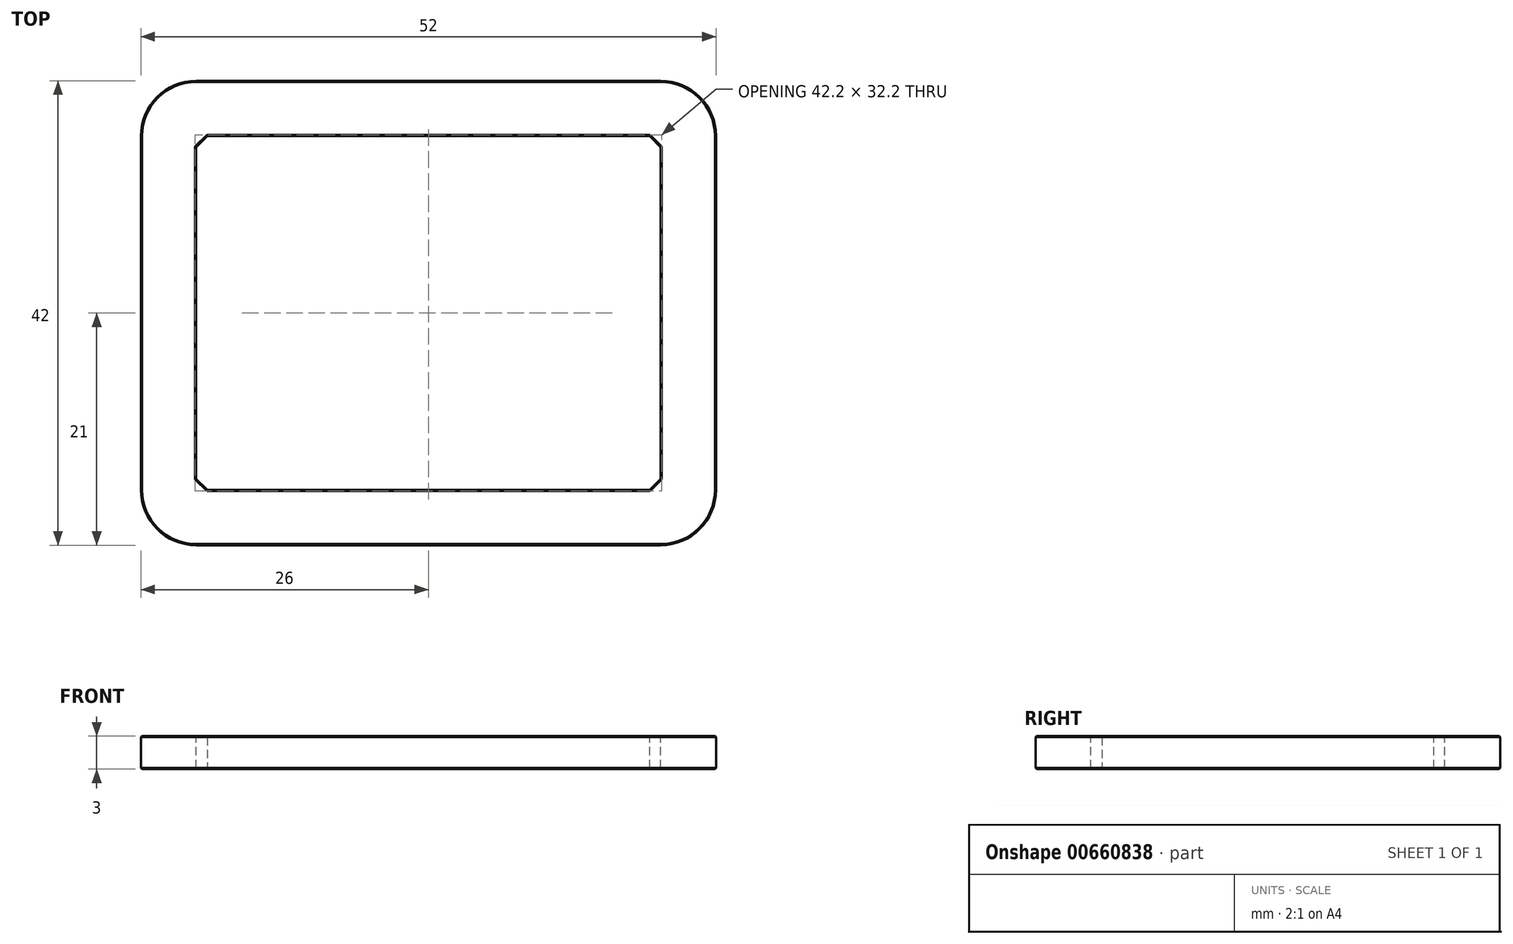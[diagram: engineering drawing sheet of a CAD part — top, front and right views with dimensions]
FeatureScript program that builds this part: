
annotation { "Feature Type Name" : "Feature", "Feature Type Description" : "" }
export const myFeature = defineFeature(function(context is Context, id is Id, definition is map)
    precondition{}
    {
        {
            var Q0;
            Q0=qCreatedBy(makeId("Top.planeOp"),FACE);
            var sketch = newSketch(context, id + "F0", { "sketchPlane" : qUnion([Q0])});
            skLineSegment(sketch, "E0.bottom", {"start": v(-26, 21) * mm, "end": v(26, 21) * mm});
            skLineSegment(sketch, "E0.top", {"start": v(-26, -21) * mm, "end": v(26, -21) * mm});
            skLineSegment(sketch, "E0.left", {"start": v(-26, 21) * mm, "end": v(-26, -21) * mm});
            skLineSegment(sketch, "E0.right", {"start": v(26, 21) * mm, "end": v(26, -21) * mm});
            skPoint(sketch, "E0.middle", {"position": v(0, 0) * mm});
            skLineSegment(sketch, "E1.bottom", {"start": v(-21, 16) * mm, "end": v(21, 16) * mm});
            skLineSegment(sketch, "E1.top", {"start": v(-21, -16) * mm, "end": v(21, -16) * mm});
            skLineSegment(sketch, "E1.left", {"start": v(-21, 16) * mm, "end": v(-21, -16) * mm});
            skLineSegment(sketch, "E1.right", {"start": v(21, 16) * mm, "end": v(21, -16) * mm});
            skSolve(sketch);
        }
        {
            var Q0;
            Q0=makeQuery(id+"F0.imprint","IMPRINT",FACE,{"disambiguationData":[TD([[makeQuery(id+"F0.imprint","IMPRINT",EDGE,{"derivedFrom":sQuery(id+"F0.wireOp",EDGE,"E0.bottom")}),-1.0]])]});
            extrude(context, id + "F1", {"entities" : qUnion([Q0]), "depth" : 3 * mm, "offsetDistance" : 25 * mm});
        }
        {
            var Q0;
            Q0=makeQuery(id+"F1.opExtrude","SWEPT_EDGE",EDGE,{"disambiguationData":[OSD([sQuery(id+"F0.wireOp",EDGE,"E0.bottom"),sQuery(id+"F0.wireOp",EDGE,"E0.left")])]});
            var Q1;
            Q1=makeQuery(id+"F1.opExtrude","SWEPT_EDGE",EDGE,{"disambiguationData":[OSD([sQuery(id+"F0.wireOp",EDGE,"E0.top"),sQuery(id+"F0.wireOp",EDGE,"E0.left")])]});
            var Q2;
            Q2=makeQuery(id+"F1.opExtrude","SWEPT_EDGE",EDGE,{"disambiguationData":[OSD([sQuery(id+"F0.wireOp",EDGE,"E0.top"),sQuery(id+"F0.wireOp",EDGE,"E0.right")])]});
            var Q3;
            Q3=makeQuery(id+"F1.opExtrude","SWEPT_EDGE",EDGE,{"disambiguationData":[OSD([sQuery(id+"F0.wireOp",EDGE,"E0.bottom"),sQuery(id+"F0.wireOp",EDGE,"E0.right")])]});
            fillet(context, id + "F2", {"entities" : qUnion([Q0, Q1, Q2, Q3]), "radius" : 5 * mm, "tangentPropagation" : true, "allowEdgeOverflow" : false});
        }
        {
            var Q0;
            Q0=makeQuery(id+"F1.opExtrude","SWEPT_EDGE",EDGE,{"disambiguationData":[OSD([sQuery(id+"F0.wireOp",EDGE,"E1.bottom"),sQuery(id+"F0.wireOp",EDGE,"E1.left")])]});
            chamfer(context, id + "F3", {"entities" : qUnion([Q0]), "chamferType" : ChamferType.TWO_OFFSETS, "width1" : 1 * mm, "oppositeDirection" : true, "width2" : 1 * mm, "tangentPropagation" : true});
        }
        {
            var Q0;
            Q0=makeQuery(id+"F1.opExtrude","SWEPT_EDGE",EDGE,{"disambiguationData":[OSD([sQuery(id+"F0.wireOp",EDGE,"E1.bottom"),sQuery(id+"F0.wireOp",EDGE,"E1.right")])]});
            var Q1;
            Q1=makeQuery(id+"F1.opExtrude","SWEPT_EDGE",EDGE,{"disambiguationData":[OSD([sQuery(id+"F0.wireOp",EDGE,"E1.top"),sQuery(id+"F0.wireOp",EDGE,"E1.right")])]});
            var Q2;
            Q2=makeQuery(id+"F1.opExtrude","SWEPT_EDGE",EDGE,{"disambiguationData":[OSD([sQuery(id+"F0.wireOp",EDGE,"E1.top"),sQuery(id+"F0.wireOp",EDGE,"E1.left")])]});
            chamfer(context, id + "F4", {"entities" : qUnion([Q0, Q1, Q2]), "width" : 1 * mm, "tangentPropagation" : true});
        }
        {
            var Q0;
            Q0=makeQuery(id+"F1.opExtrude","CAP_FACE",FACE,{"disambiguationData":[OSD([sQuery(id+"F0.wireOp",EDGE,"E0.bottom"),sQuery(id+"F0.wireOp",EDGE,"E0.top"),sQuery(id+"F0.wireOp",EDGE,"E0.left"),sQuery(id+"F0.wireOp",EDGE,"E0.right"),sQuery(id+"F0.wireOp",EDGE,"E1.bottom"),sQuery(id+"F0.wireOp",EDGE,"E1.top"),sQuery(id+"F0.wireOp",EDGE,"E1.left"),sQuery(id+"F0.wireOp",EDGE,"E1.right")])],"isStart":false});
            var Q1;
            Q1=makeQuery(id+"F1.opExtrude","CAP_FACE",FACE,{"disambiguationData":[OSD([sQuery(id+"F0.wireOp",EDGE,"E0.bottom"),sQuery(id+"F0.wireOp",EDGE,"E0.top"),sQuery(id+"F0.wireOp",EDGE,"E0.left"),sQuery(id+"F0.wireOp",EDGE,"E0.right"),sQuery(id+"F0.wireOp",EDGE,"E1.bottom"),sQuery(id+"F0.wireOp",EDGE,"E1.top"),sQuery(id+"F0.wireOp",EDGE,"E1.left"),sQuery(id+"F0.wireOp",EDGE,"E1.right")])],"isStart":true});
            chamfer(context, id + "F5", {"entities" : qUnion([Q0, Q1]), "width" : 0.1 * mm, "tangentPropagation" : true});
        }
    });
